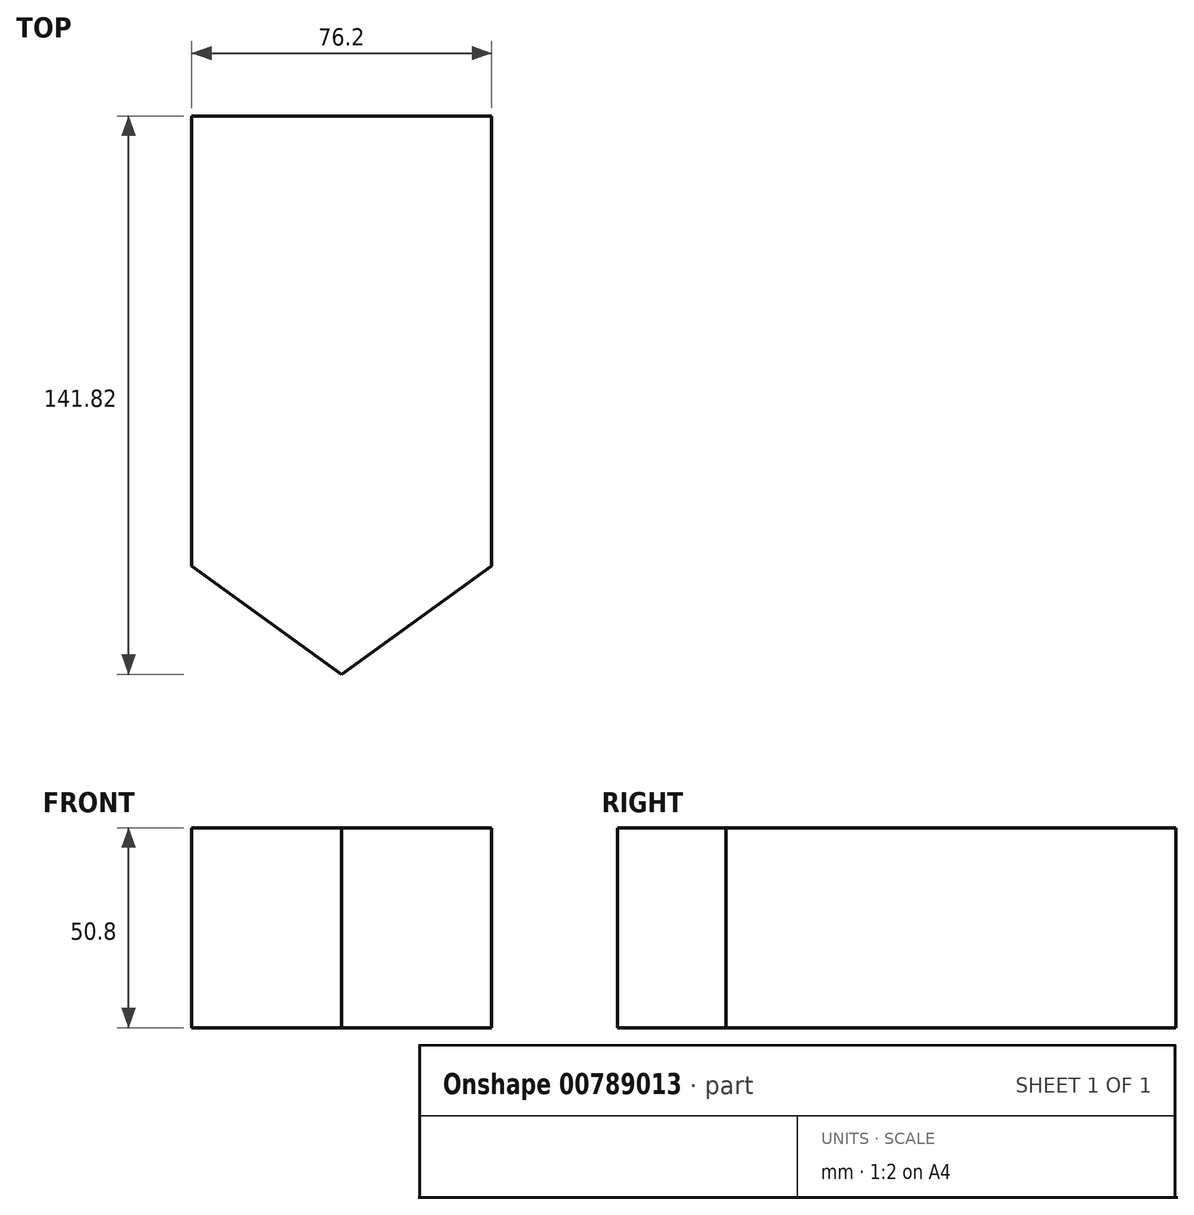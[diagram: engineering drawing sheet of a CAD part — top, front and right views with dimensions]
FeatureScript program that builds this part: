
annotation { "Feature Type Name" : "Feature", "Feature Type Description" : "" }
export const myFeature = defineFeature(function(context is Context, id is Id, definition is map)
    precondition{}
    {
        {
            var Q0;
            Q0=qCreatedBy(makeId("Top.planeOp"),FACE);
            var sketch = newSketch(context, id + "F0", { "sketchPlane" : qUnion([Q0])});
            skLineSegment(sketch, "E0", {"start": v(-18.99, 133.28) * mm, "end": v(-18.99, 18.98) * mm});
            skLineSegment(sketch, "E1", {"start": v(-18.99, 133.28) * mm, "end": v(57.21, 133.28) * mm});
            skLineSegment(sketch, "E2", {"start": v(57.21, 133.28) * mm, "end": v(57.21, 18.98) * mm});
            skLineSegment(sketch, "E3", {"start": v(-18.99, 18.98) * mm, "end": v(19.11, -8.54) * mm});
            skLineSegment(sketch, "E4", {"start": v(19.11, -8.54) * mm, "end": v(57.21, 18.98) * mm});
            skSolve(sketch);
        }
        {
            var Q0;
            Q0 = qSketchRegion(id + "F0", true);
            extrude(context, id + "F1", {"entities" : qUnion([Q0]), "depth" : 50.8 * mm, "offsetDistance" : 25.4 * mm});
        }
    });
